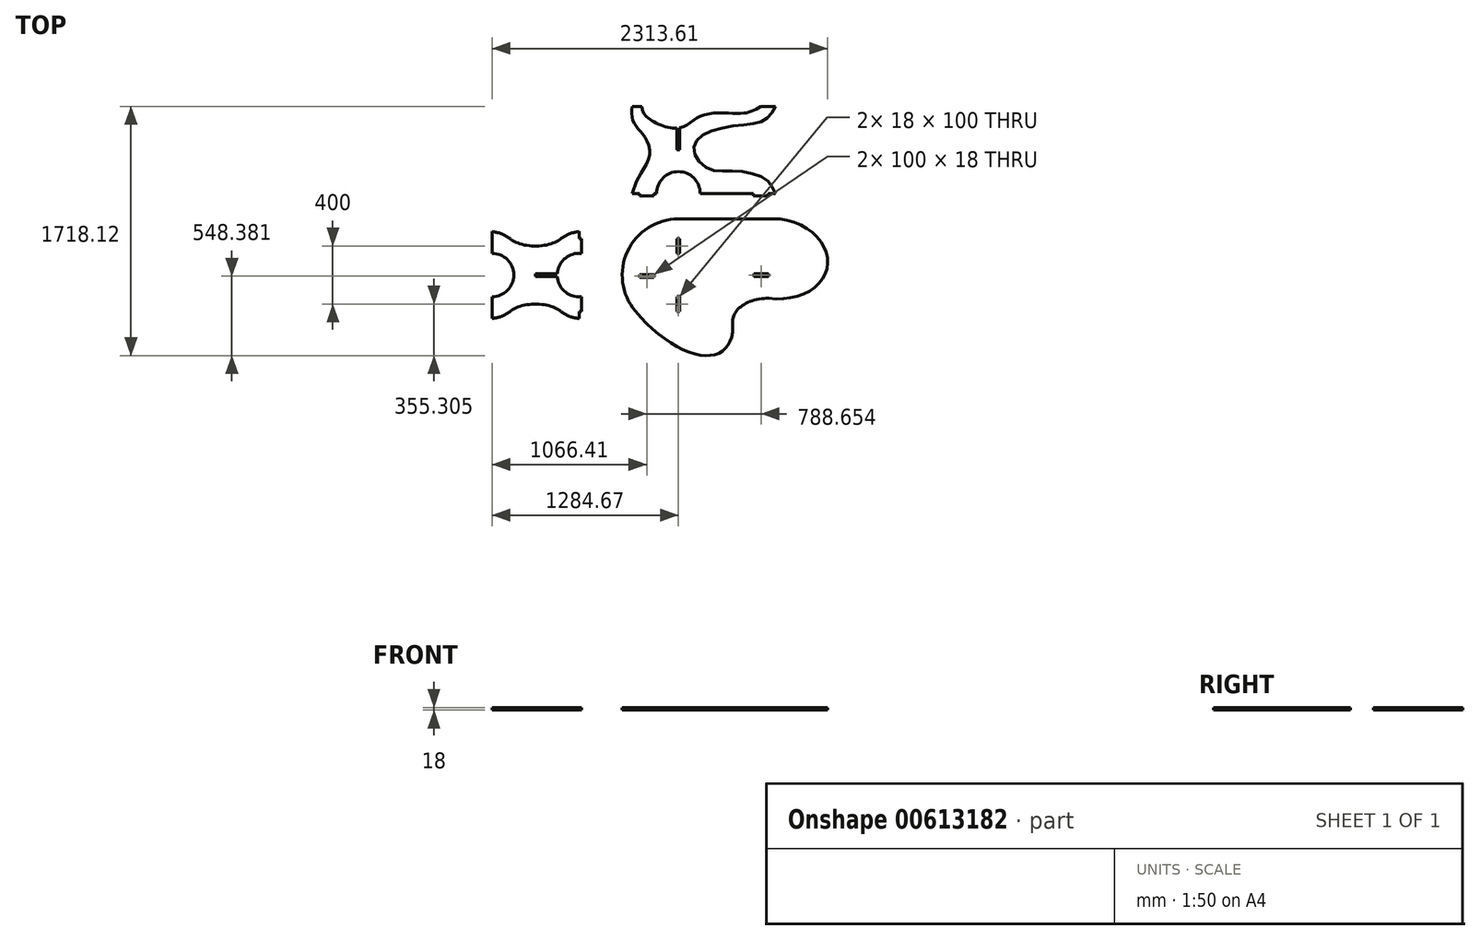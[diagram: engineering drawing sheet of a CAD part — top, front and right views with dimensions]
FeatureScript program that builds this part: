
annotation { "Feature Type Name" : "Feature", "Feature Type Description" : "" }
export const myFeature = defineFeature(function(context is Context, id is Id, definition is map)
    precondition{}
    {
        {
            var Q0;
            Q0=qCreatedBy(makeId("Top.planeOp"),FACE);
            var sketch = newSketch(context, id + "F0", { "sketchPlane" : qUnion([Q0])});
            skLineSegment(sketch, "E0", {"start": v(-3948.23, 571.92) * mm, "end": v(-3548.23, 571.92) * mm});
            skPoint(sketch, "E1.visualSharp", {"position": v(-3348.23, 571.92) * mm});
            skArc(sketch, "E2", {"start": v(-4248.23, 571.92) * mm, "mid": v(-4599.3, 348.05) * mm, "end": v(-4544.42, -64.68) * mm});
            skLineSegment(sketch, "E3", {"start": v(-3948.23, 571.92) * mm, "end": v(-4248.23, 571.92) * mm});
            skPoint(sketch, "E4.orphan", {"position": v(-4624.74, 99.26) * mm});
            skEllipticalArc(sketch, "E5", {});
            skEllipticalArc(sketch, "E6", {});
            skEllipticalArc(sketch, "E7", {});
            skPoint(sketch, "E8.orphan", {"position": v(-4324.74, -194.85) * mm});
            skLineSegment(sketch, "E9", {"start": v(-4248.23, 334.71) * mm, "end": v(-4239.23, 334.71) * mm});
            skLineSegment(sketch, "E10", {"start": v(-4239.23, 334.71) * mm, "end": v(-4239.23, 434.71) * mm});
            skLineSegment(sketch, "E11", {"start": v(-4239.23, 434.71) * mm, "end": v(-4257.23, 434.71) * mm});
            skLineSegment(sketch, "E12", {"start": v(-4257.23, 434.71) * mm, "end": v(-4257.23, 334.71) * mm});
            skLineSegment(sketch, "E13", {"start": v(-4257.23, 334.71) * mm, "end": v(-4248.23, 334.71) * mm});
            skLineSegment(sketch, "E14.MirrorCS", {"start": v(-4239.23, 34.71) * mm, "end": v(-4239.23, -65.29) * mm});
            skLineSegment(sketch, "E15.MirrorCS", {"start": v(-4257.23, -65.29) * mm, "end": v(-4257.23, 34.71) * mm});
            skLineSegment(sketch, "E16.MirrorCS", {"start": v(-4239.23, -65.29) * mm, "end": v(-4257.23, -65.29) * mm});
            skLineSegment(sketch, "E17.MirrorCS", {"start": v(-4257.23, 34.71) * mm, "end": v(-4248.23, 34.71) * mm});
            skLineSegment(sketch, "E18.MirrorCS", {"start": v(-4248.23, 34.71) * mm, "end": v(-4239.23, 34.71) * mm});
            skLineSegment(sketch, "E19", {"start": v(-4932.9, 484.71) * mm, "end": v(-4932.9, 434.71) * mm});
            skLineSegment(sketch, "E20", {"start": v(-5532.9, -115.29) * mm, "end": v(-5532.9, 34.71) * mm});
            skArc(sketch, "E21", {"start": v(-4932.9, 334.71) * mm, "mid": v(-5035.74, 293.92) * mm, "end": v(-5082.63, 193.71) * mm});
            skLineSegment(sketch, "E22", {"start": v(-4932.9, 334.71) * mm, "end": v(-4914.9, 334.71) * mm});
            skLineSegment(sketch, "E23", {"start": v(-4914.9, 334.71) * mm, "end": v(-4914.9, 434.71) * mm});
            skLineSegment(sketch, "E24", {"start": v(-4914.9, 434.71) * mm, "end": v(-4932.9, 434.71) * mm});
            skLineSegment(sketch, "E25.trimOffspring", {"start": v(-4932.9, -65.29) * mm, "end": v(-4932.9, -115.29) * mm});
            skEllipticalArc(sketch, "E26", {});
            skFitSpline(sketch, "E27", {"points": [v(-4932.9, 484.71) * mm, v(-5004.7, 466.97) * mm, v(-5071.87, 425.41) * mm], "startDerivative": vector(-149.36, -24.89) * mm, "endDerivative": vector(-128.77, -93.21) * mm});
            skFitSpline(sketch, "E28.MirrorCS", {"points": [v(-5532.9, 484.71) * mm, v(-5461.12, 466.97) * mm, v(-5393.94, 425.41) * mm], "startDerivative": vector(149.36, -24.89) * mm, "endDerivative": vector(128.77, -93.21) * mm});
            skEllipticalArc(sketch, "E29.MirrorCS", {});
            skFitSpline(sketch, "E30.MirrorCS", {"points": [v(-5532.9, -115.29) * mm, v(-5461.12, -97.54) * mm, v(-5393.94, -55.98) * mm], "startDerivative": vector(149.36, 24.89) * mm, "endDerivative": vector(128.77, 93.21) * mm});
            skFitSpline(sketch, "E31.MirrorCS", {"points": [v(-4932.9, -115.29) * mm, v(-5004.7, -97.54) * mm, v(-5071.87, -55.98) * mm], "startDerivative": vector(-149.36, 24.89) * mm, "endDerivative": vector(-128.77, 93.21) * mm});
            skLineSegment(sketch, "E32", {"start": v(-4566.52, 747.53) * mm, "end": v(-4516.52, 747.53) * mm});
            skLineSegment(sketch, "E33", {"start": v(-4516.52, 747.53) * mm, "end": v(-4516.52, 729.53) * mm});
            skLineSegment(sketch, "E34", {"start": v(-4516.52, 729.53) * mm, "end": v(-4416.52, 729.53) * mm});
            skLineSegment(sketch, "E35", {"start": v(-4416.52, 729.53) * mm, "end": v(-4416.52, 747.53) * mm});
            skLineSegment(sketch, "E36.MirrorCS", {"start": v(-3729.94, 729.53) * mm, "end": v(-3729.94, 747.53) * mm});
            skLineSegment(sketch, "E37.MirrorCS", {"start": v(-3629.94, 747.53) * mm, "end": v(-3629.94, 729.53) * mm});
            skFitSpline(sketch, "E38", {"points": [v(-3579.94, 747.53) * mm, v(-3647.4, 845.18) * mm, v(-3854.83, 900.94) * mm, v(-4048.88, 921) * mm, v(-4141.68, 1047.53) * mm, v(-4080.1, 1148.5) * mm, v(-3825.84, 1217.65) * mm, v(-3651.87, 1253.34) * mm, v(-3579.94, 1347.53) * mm], "startDerivative": vector(-454.33, 1018.23) * mm, "endDerivative": vector(552.02, 1044.77) * mm});
            skLineSegment(sketch, "E39", {"start": v(-3579.94, 1347.53) * mm, "end": v(-3679.94, 1347.53) * mm});
            skFitSpline(sketch, "E40", {"points": [v(-3679.94, 1347.53) * mm, v(-3751.82, 1310.66) * mm, v(-3853.1, 1299.41) * mm, v(-4093.16, 1282.53) * mm, v(-4248.23, 1197.53) * mm, v(-4470.14, 1278.78) * mm, v(-4500.15, 1347.53) * mm], "startDerivative": vector(-566.04, -339.72) * mm, "endDerivative": vector(-76.28, 554.63) * mm});
            skFitSpline(sketch, "E41", {"points": [v(-4566.52, 747.53) * mm, v(-4522.56, 858.86) * mm, v(-4448.3, 1006.94) * mm, v(-4478.57, 1136.35) * mm, v(-4530.33, 1198.37) * mm, v(-4566.52, 1265.89) * mm, v(-4566.52, 1347.53) * mm], "startDerivative": vector(189.84, 616.3) * mm, "endDerivative": vector(61.65, 575.62) * mm});
            skLineSegment(sketch, "E42.trimOffspring", {"start": v(-3679.94, 1347.53) * mm, "end": v(-3579.94, 1347.53) * mm});
            skLineSegment(sketch, "E43", {"start": v(-4566.52, 1347.53) * mm, "end": v(-4500.15, 1347.53) * mm});
            skLineSegment(sketch, "E44", {"start": v(-4416.52, 747.53) * mm, "end": v(-4398.23, 747.53) * mm});
            skLineSegment(sketch, "E45.trimOffspring", {"start": v(-3883.97, 747.53) * mm, "end": v(-3729.94, 747.53) * mm});
            skPoint(sketch, "E46.endSnap0", {"position": v(-5532.9, 184.71) * mm});
            skArc(sketch, "E47", {"start": v(-5532.9, 34.71) * mm, "mid": v(-5382.9, 184.71) * mm, "end": v(-5532.9, 334.71) * mm});
            skArc(sketch, "E48", {"start": v(-4098.23, 747.53) * mm, "mid": v(-4248.23, 897.53) * mm, "end": v(-4398.23, 747.53) * mm});
            skLineSegment(sketch, "E49", {"start": v(-3883.97, 747.53) * mm, "end": v(-4098.23, 747.53) * mm});
            skPoint(sketch, "E50.start.orphan", {"position": v(-4248.23, 897.53) * mm});
            skLineSegment(sketch, "E51.trimOffspring", {"start": v(-5532.9, 334.71) * mm, "end": v(-5532.9, 484.71) * mm});
            skLineSegment(sketch, "E52", {"start": v(-5232.9, 193.71) * mm, "end": v(-5232.9, 175.71) * mm});
            skLineSegment(sketch, "E53", {"start": v(-5232.9, 193.71) * mm, "end": v(-5082.63, 193.71) * mm});
            skLineSegment(sketch, "E54", {"start": v(-5082.63, 175.71) * mm, "end": v(-5232.9, 175.71) * mm});
            skArc(sketch, "E55.trimOffspring", {"start": v(-5082.63, 175.71) * mm, "mid": v(-5035.74, 75.51) * mm, "end": v(-4932.9, 34.71) * mm});
            skLineSegment(sketch, "E56", {"start": v(-4248.23, 1047.53) * mm, "end": v(-4257.23, 1047.53) * mm});
            skLineSegment(sketch, "E57", {"start": v(-4257.23, 1047.53) * mm, "end": v(-4257.23, 1196.6) * mm});
            skLineSegment(sketch, "E58", {"start": v(-4239.23, 1199.13) * mm, "end": v(-4239.23, 1047.53) * mm});
            skLineSegment(sketch, "E59", {"start": v(-4239.23, 1047.53) * mm, "end": v(-4248.23, 1047.53) * mm});
            skLineSegment(sketch, "E60.MirrorCS", {"start": v(-4932.9, 34.71) * mm, "end": v(-4914.9, 34.71) * mm});
            skLineSegment(sketch, "E61.MirrorCS", {"start": v(-4914.9, 34.71) * mm, "end": v(-4914.9, -65.29) * mm});
            skLineSegment(sketch, "E62.MirrorCS", {"start": v(-4914.9, -65.29) * mm, "end": v(-4932.9, -65.29) * mm});
            skPoint(sketch, "E63.end.orphan", {"position": v(-3579.94, 174.96) * mm});
            skLineSegment(sketch, "E64.MirrorCS", {"start": v(-4516.5, 168.8) * mm, "end": v(-4416.5, 168.8) * mm});
            skLineSegment(sketch, "E65.MirrorCS", {"start": v(-4516.5, 186.8) * mm, "end": v(-4516.5, 168.8) * mm});
            skLineSegment(sketch, "E66.MirrorCS", {"start": v(-4416.5, 186.8) * mm, "end": v(-4516.5, 186.8) * mm});
            skLineSegment(sketch, "E67.trimOffspring", {"start": v(-3629.94, 747.53) * mm, "end": v(-3579.94, 747.53) * mm});
            skPoint(sketch, "E68.endSnap0", {"position": v(-4466.5, 186.8) * mm});
            skLineSegment(sketch, "E69", {"start": v(-4416.5, 186.8) * mm, "end": v(-4416.5, 168.8) * mm});
            skLineSegment(sketch, "E70", {"start": v(-3677.84, 193.71) * mm, "end": v(-3627.84, 193.71) * mm});
            skLineSegment(sketch, "E71", {"start": v(-3627.84, 193.71) * mm, "end": v(-3627.84, 175.71) * mm});
            skLineSegment(sketch, "E72", {"start": v(-3627.84, 175.71) * mm, "end": v(-3727.84, 175.71) * mm});
            skLineSegment(sketch, "E73", {"start": v(-3727.84, 175.71) * mm, "end": v(-3727.84, 193.71) * mm});
            skLineSegment(sketch, "E74", {"start": v(-3727.84, 193.71) * mm, "end": v(-3677.84, 193.71) * mm});
            skLineSegment(sketch, "E75", {"start": v(-3729.94, 729.53) * mm, "end": v(-3629.94, 729.53) * mm});
            const initialGuessF0  = {"E5": [-3.624744415283206, -0.133532573329782, 0, 1, 0.15846771927731645, 0.24952230938477182, 6.283185307179586, 1.5707963267948966], "E6": [-3.586488766068417, 0.2984253336943529, -0.13853072310714565, -0.9903581366129183, 0.27615281546751425, 0.3687602717267947, 6.283185307179586, 3.141592653589793], "E7": [-4.324744415283204, 0.14199063181877136, 0.6306186014098706, -0.7760928936382929, 0.6135085232042197, 0.30100996084626147, 4.748036428997269, 0.6239450032915048], "E26": [-5.232904148101807, 0.48471492528915405, 1, 0, 0.2, 0.1, 3.716872491789872, 5.7079054689783], "E29.MirrorCS": [-5.232904148101807, -0.11528507471084537, 1, 0, 0.2, 0.1, 0.5752798382012863, 2.5663128153897152]};
            skSetInitialGuess(sketch, initialGuessF0);
            skSolve(sketch);
        }
        {
            var Q0;
            {var subQ14=sQuery(id+"F0.wireOp",EDGE,"E19");Q0=makeQuery(id+"F0.imprint","IMPRINT",FACE,{"disambiguationData":[TD([[makeQuery(id+"F0.imprint","IMPRINT",EDGE,{"derivedFrom":subQ14}),-1.0]])]});}
            extrude(context, id + "F1", {"entities" : qUnion([Q0]), "depth" : 18 * mm, "offsetDistance" : 25 * mm});
        }
        {
            var Q0;
            Q0=makeQuery(id+"F0.imprint","IMPRINT",FACE,{"disambiguationData":[TD([[makeQuery(id+"F0.imprint","IMPRINT",EDGE,{"derivedFrom":sQuery(id+"F0.wireOp",EDGE,"E0")}),-1.0]])]});
            var Q1;
            Q1=makeQuery(id+"F0.imprint","IMPRINT",FACE,{"disambiguationData":[TD([[makeQuery(id+"F0.imprint","IMPRINT",EDGE,{"derivedFrom":sQuery(id+"F0.wireOp",EDGE,"E32")}),1.0]])]});
            extrude(context, id + "F2", {"entities" : qUnion([Q0, Q1]), "depth" : 18 * mm, "offsetDistance" : 25 * mm});
        }
    });
